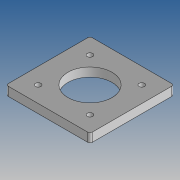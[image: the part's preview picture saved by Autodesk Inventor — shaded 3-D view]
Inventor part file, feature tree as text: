
AUTODESK INVENTOR PART (.ipt)
format: ipt  version: 2017 (Build 210142000, 142)  size: 104,448 bytes
history: native  units: mm
features: extrude x1, sketch x1
ambient origin geometry x8: Origin, YZ Plane, XZ Plane, XY Plane, X Axis, Y Axis, Z Axis, Center Point
bodies: Body1 (feature_tree)
feature tree (2):
  extrude  "Extrusión1"  Depth=2.0mm
  sketch  "Boceto1"  dims[d0=76.4mm d1=2.0mm d2=5.0mm d3=61.609459mm d4=40.0mm d5=8.0mm d6=0.0mm d23=47.1mm]
